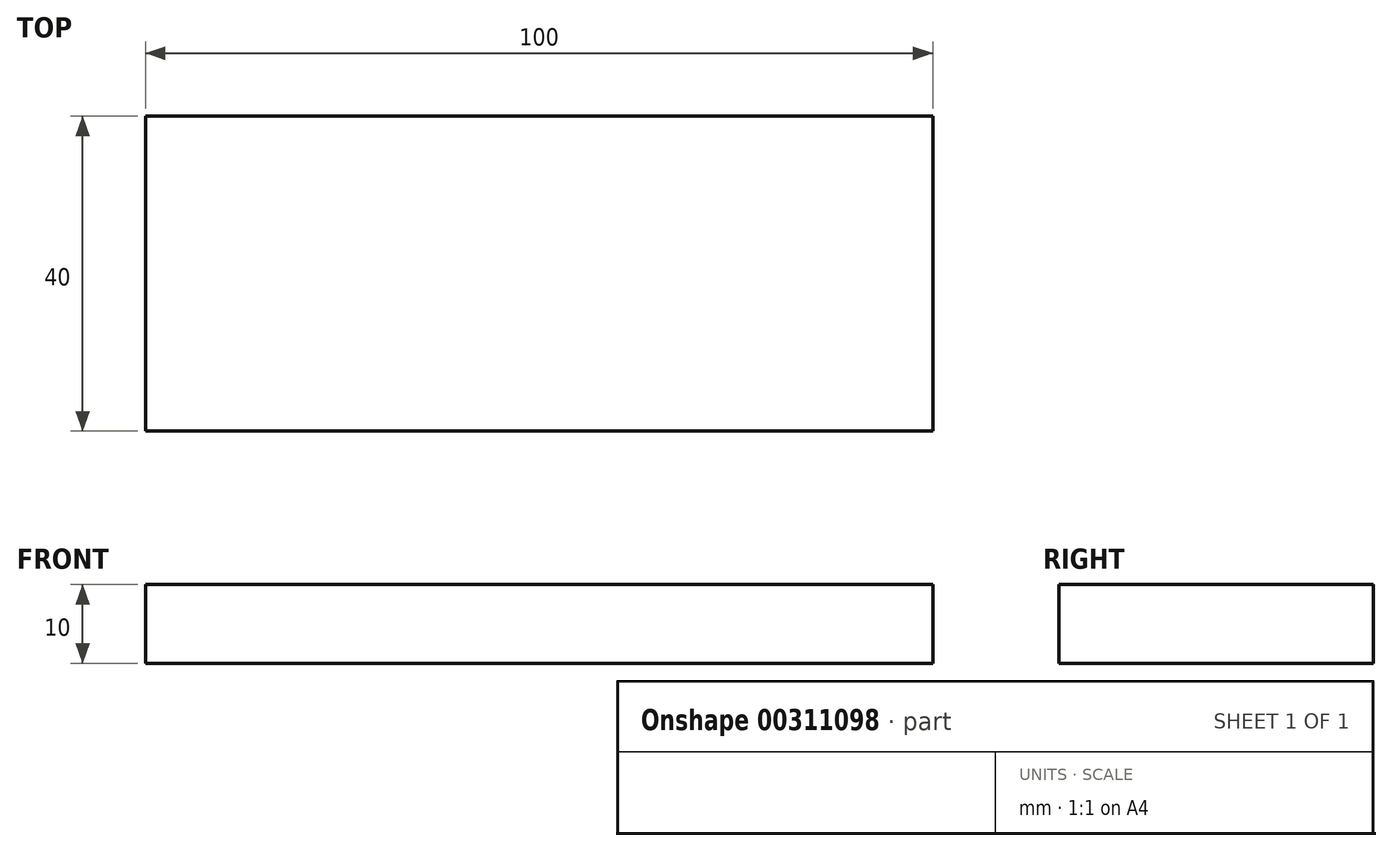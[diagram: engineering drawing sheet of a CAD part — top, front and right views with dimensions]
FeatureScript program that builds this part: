
annotation { "Feature Type Name" : "Feature", "Feature Type Description" : "" }
export const myFeature = defineFeature(function(context is Context, id is Id, definition is map)
    precondition{}
    {
        {
            var Q0;
            Q0=qCreatedBy(makeId("Top.planeOp"),FACE);
            var sketch = newSketch(context, id + "F0", { "sketchPlane" : qUnion([Q0])});
            skLineSegment(sketch, "E0.bottom", {"start": v(0, 0) * mm, "end": v(-100, 0) * mm});
            skLineSegment(sketch, "E0.top", {"start": v(0, 40) * mm, "end": v(-100, 40) * mm});
            skLineSegment(sketch, "E0.left", {"start": v(0, 0) * mm, "end": v(0, 40) * mm});
            skLineSegment(sketch, "E0.right", {"start": v(-100, 0) * mm, "end": v(-100, 40) * mm});
            skSolve(sketch);
        }
        {
            var Q0;
            Q0=makeQuery(id+"F0.imprint","IMPRINT",FACE,{"disambiguationData":[TD([[makeQuery(id+"F0.imprint","IMPRINT",EDGE,{"derivedFrom":sQuery(id+"F0.wireOp",EDGE,"E0.bottom")}),-1.0]])]});
            extrude(context, id + "F1", {"entities" : qUnion([Q0]), "depth" : 10 * mm});
        }
    });
